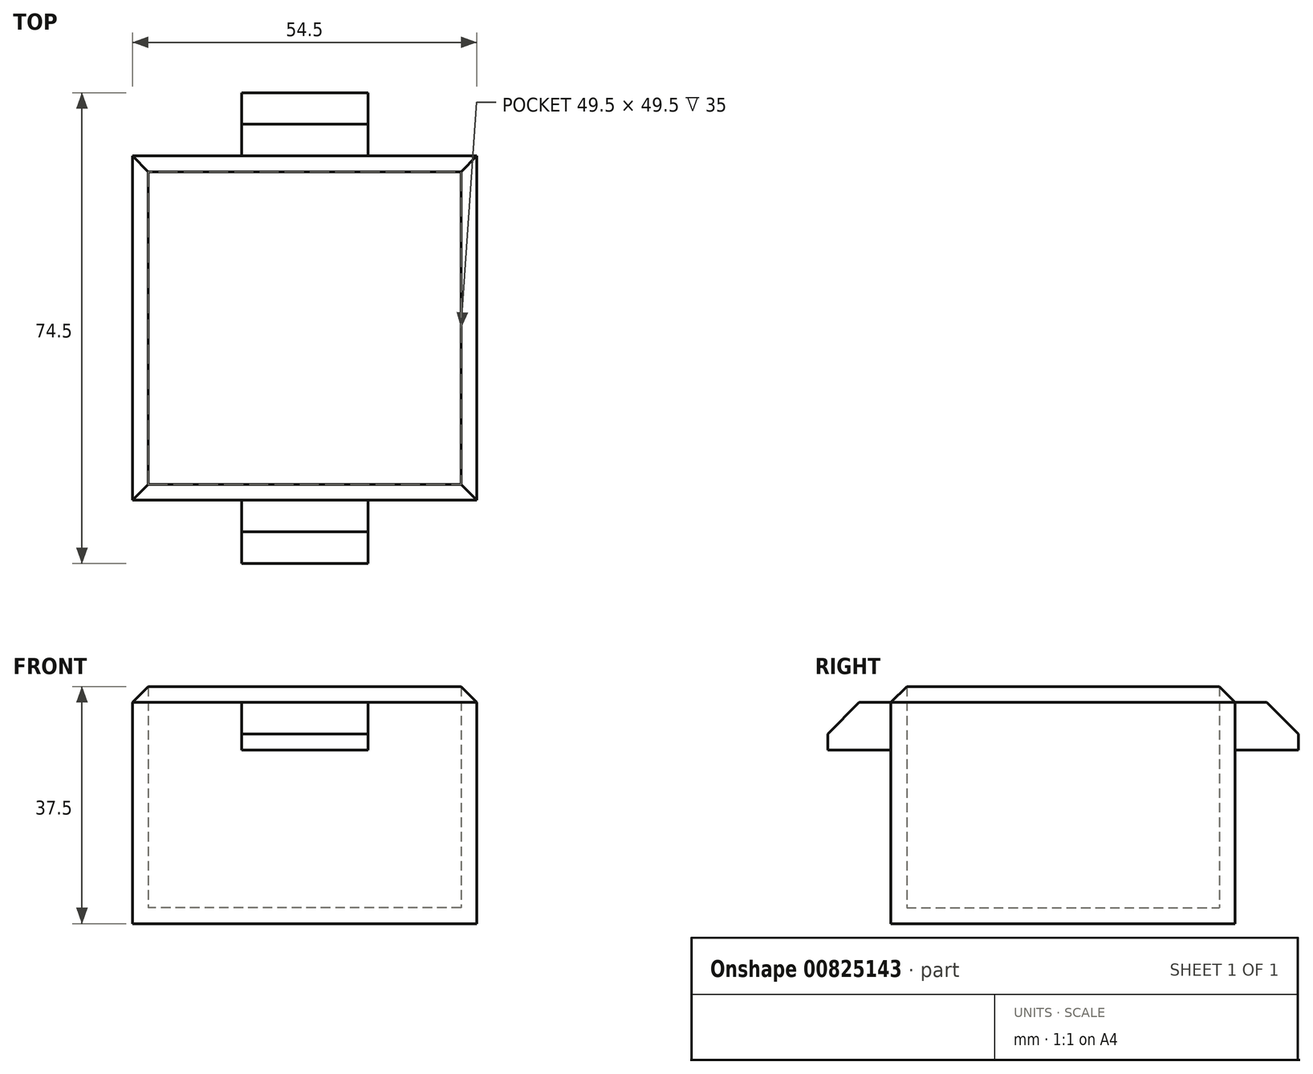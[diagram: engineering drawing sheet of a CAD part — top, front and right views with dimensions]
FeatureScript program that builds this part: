
annotation { "Feature Type Name" : "Feature", "Feature Type Description" : "" }
export const myFeature = defineFeature(function(context is Context, id is Id, definition is map)
    precondition{}
    {
        {
            var Q0;
            Q0=qCreatedBy(makeId("Front.planeOp"),FACE);
            var sketch = newSketch(context, id + "F0", { "sketchPlane" : qUnion([Q0])});
            skLineSegment(sketch, "E0.bottom", {"start": v(27.25, 10) * mm, "end": v(-27.25, 10) * mm});
            skLineSegment(sketch, "E0.top", {"start": v(27.25, -10) * mm, "end": v(-27.25, -10) * mm});
            skLineSegment(sketch, "E0.left", {"start": v(27.25, 10) * mm, "end": v(27.25, -10) * mm});
            skLineSegment(sketch, "E0.right", {"start": v(-27.25, 10) * mm, "end": v(-27.25, -10) * mm});
            skPoint(sketch, "E0.middle", {"position": v(0, 0) * mm});
            skSolve(sketch);
        }
        {
            var Q0;
            Q0=makeQuery(id+"F0.imprint","IMPRINT",FACE,{"disambiguationData":[TD([[makeQuery(id+"F0.imprint","IMPRINT",EDGE,{"derivedFrom":sQuery(id+"F0.wireOp",EDGE,"E0.bottom")}),1.0]])]});
            extrude(context, id + "F1", {"entities" : qUnion([Q0]), "depth" : 54.5 * mm, "offsetDistance" : 25 * mm});
        }
        {
            var Q0;
            Q0=makeQuery(id+"F1.opExtrude","SWEPT_FACE",FACE,{"disambiguationData":[OSD([sQuery(id+"F0.wireOp",EDGE,"E0.bottom")])]});
            extrude(context, id + "F2", {"entities" : qUnion([Q0]), "operationType" : NewBodyOperationType.ADD, "depth" : 20 * mm, "offsetDistance" : 25 * mm});
        }
        {
            var Q0;
            Q0=makeQuery(id+"F2.opExtrude","CAP_FACE",FACE,{"disambiguationData":[OSD([sQuery(id+"F0.wireOp",EDGE,"E0.bottom")])],"isStart":false});
            shell(context, id + "F3", {"entities" : qUnion([Q0]), "thickness" : 2.5 * mm});
        }
        {
            var Q0;
            {var subQ0=sQuery(id+"F0.wireOp",EDGE,"E0.bottom");Q0=makeQuery(id+"F2.boolean.opBoolean","MERGE",FACE,{"derivedFrom":[makeQuery(id+"F1.opExtrude","CAP_FACE",FACE,{"disambiguationData":[OSD([subQ0,sQuery(id+"F0.wireOp",EDGE,"E0.top"),sQuery(id+"F0.wireOp",EDGE,"E0.left"),sQuery(id+"F0.wireOp",EDGE,"E0.right")])],"isStart":false}),makeQuery(id+"F2.opExtrude","SWEPT_FACE",FACE,{"disambiguationData":[OSD([subQ0]),TDD([makeQuery(id+"F1.opExtrude","CAP_EDGE",EDGE,{"disambiguationData":[OSD([subQ0])],"isStart":false})])]})]});}
            var sketch = newSketch(context, id + "F4", { "sketchPlane" : qUnion([Q0])});
            skLineSegment(sketch, "E1", {"start": v(0, 0) * mm, "end": v(0, 30) * mm});
            skLineSegment(sketch, "E2", {"start": v(0, 30) * mm, "end": v(0, 25) * mm});
            skLineSegment(sketch, "E3", {"start": v(0, 25) * mm, "end": v(-10, 25) * mm});
            skLineSegment(sketch, "E4", {"start": v(-10, 25) * mm, "end": v(10, 25) * mm});
            skLineSegment(sketch, "E5", {"start": v(10, 25) * mm, "end": v(10, 17.5) * mm});
            skLineSegment(sketch, "E6", {"start": v(10, 17.5) * mm, "end": v(-10, 17.5) * mm});
            skLineSegment(sketch, "E7", {"start": v(-10, 17.5) * mm, "end": v(-10, 25) * mm});
            skSolve(sketch);
        }
        {
            var Q0;
            {var subQ5=sQuery(id+"F4.wireOp",EDGE,"E7");Q0=makeQuery(id+"F4.imprint","IMPRINT",FACE,{"disambiguationData":[TD([[makeQuery(id+"F4.imprint","IMPRINT",EDGE,{"derivedFrom":subQ5}),-1.0]])]});}
            var Q1;
            {var subQ5=sQuery(id+"F4.wireOp",EDGE,"E5");Q1=makeQuery(id+"F4.imprint","IMPRINT",FACE,{"disambiguationData":[TD([[makeQuery(id+"F4.imprint","IMPRINT",EDGE,{"derivedFrom":subQ5}),-1.0]])]});}
            extrude(context, id + "F5", {"entities" : qUnion([Q0, Q1]), "operationType" : NewBodyOperationType.ADD, "depth" : 10 * mm, "offsetDistance" : 25 * mm});
        }
        {
            var Q0;
            {var subQ0=sQuery(id+"F0.wireOp",EDGE,"E0.bottom");Q0=makeQuery(id+"F2.boolean.opBoolean","MERGE",FACE,{"derivedFrom":[makeQuery(id+"F1.opExtrude","CAP_FACE",FACE,{"disambiguationData":[OSD([subQ0,sQuery(id+"F0.wireOp",EDGE,"E0.top"),sQuery(id+"F0.wireOp",EDGE,"E0.left"),sQuery(id+"F0.wireOp",EDGE,"E0.right")])],"isStart":true}),makeQuery(id+"F2.opExtrude","SWEPT_FACE",FACE,{"disambiguationData":[OSD([subQ0]),TDD([makeQuery(id+"F1.opExtrude","CAP_EDGE",EDGE,{"disambiguationData":[OSD([subQ0])],"isStart":true})])]})]});}
            var sketch = newSketch(context, id + "F6", { "sketchPlane" : qUnion([Q0])});
            skLineSegment(sketch, "E8", {"start": v(0, 0) * mm, "end": v(0, 30) * mm});
            skLineSegment(sketch, "E9", {"start": v(0, 30) * mm, "end": v(0, 25) * mm});
            skLineSegment(sketch, "E10.bottom", {"start": v(0, 25) * mm, "end": v(-10, 25) * mm});
            skLineSegment(sketch, "E10.top", {"start": v(0, 17.5) * mm, "end": v(-10, 17.5) * mm});
            skLineSegment(sketch, "E10.left", {"start": v(0, 25) * mm, "end": v(0, 17.5) * mm});
            skLineSegment(sketch, "E10.right", {"start": v(-10, 25) * mm, "end": v(-10, 17.5) * mm});
            skLineSegment(sketch, "E11.bottom", {"start": v(0, 17.5) * mm, "end": v(10, 17.5) * mm});
            skLineSegment(sketch, "E11.top", {"start": v(0, 25) * mm, "end": v(10, 25) * mm});
            skLineSegment(sketch, "E11.left", {"start": v(0, 17.5) * mm, "end": v(0, 25) * mm});
            skLineSegment(sketch, "E11.right", {"start": v(10, 17.5) * mm, "end": v(10, 25) * mm});
            skSolve(sketch);
        }
        {
            var Q0;
            Q0=makeQuery(id+"F6.imprint","IMPRINT",FACE,{"disambiguationData":[TD([[makeQuery(id+"F6.imprint","IMPRINT",EDGE,{"derivedFrom":sQuery(id+"F6.wireOp",EDGE,"E10.bottom")}),1.0]])]});
            var Q1;
            Q1=makeQuery(id+"F6.imprint","IMPRINT",FACE,{"disambiguationData":[TD([[makeQuery(id+"F6.imprint","IMPRINT",EDGE,{"derivedFrom":sQuery(id+"F6.wireOp",EDGE,"E11.bottom")}),1.0]])]});
            extrude(context, id + "F7", {"entities" : qUnion([Q0, Q1]), "operationType" : NewBodyOperationType.ADD, "depth" : 10 * mm, "offsetDistance" : 25 * mm});
        }
        {
            var Q0;
            Q0=makeQuery(id+"F7.opExtrude","CAP_EDGE",EDGE,{"disambiguationData":[OSD([sQuery(id+"F6.wireOp",EDGE,"E10.bottom"),sQuery(id+"F6.wireOp",EDGE,"E11.top")])],"isStart":false});
            var Q1;
            Q1=makeQuery(id+"F5.opExtrude","CAP_EDGE",EDGE,{"disambiguationData":[OSD([sQuery(id+"F4.wireOp",EDGE,"E4")])],"isStart":false});
            var Q2;
            {var subQ0=sQuery(id+"F0.wireOp",EDGE,"E0.bottom");Q2=makeQuery(id+"F2.opExtrude","CAP_EDGE",EDGE,{"disambiguationData":[OSD([subQ0]),TDD([makeQuery(id+"F1.opExtrude","CAP_EDGE",EDGE,{"disambiguationData":[OSD([subQ0])],"isStart":true})])],"isStart":false});}
            var Q3;
            Q3=makeQuery(id+"F2.opExtrude","CAP_EDGE",EDGE,{"disambiguationData":[OSD([sQuery(id+"F0.wireOp",EDGE,"E0.bottom"),sQuery(id+"F0.wireOp",EDGE,"E0.right")])],"isStart":false});
            var Q4;
            {var subQ0=sQuery(id+"F0.wireOp",EDGE,"E0.bottom");Q4=makeQuery(id+"F2.opExtrude","CAP_EDGE",EDGE,{"disambiguationData":[OSD([subQ0]),TDD([makeQuery(id+"F1.opExtrude","CAP_EDGE",EDGE,{"disambiguationData":[OSD([subQ0])],"isStart":false})])],"isStart":false});}
            var Q5;
            Q5=makeQuery(id+"F2.opExtrude","CAP_EDGE",EDGE,{"disambiguationData":[OSD([sQuery(id+"F0.wireOp",EDGE,"E0.bottom"),sQuery(id+"F0.wireOp",EDGE,"E0.left")])],"isStart":false});
            chamfer(context, id + "F8", {"entities" : qUnion([Q0, Q1, Q2, Q3, Q4, Q5]), "width" : 5 * mm, "tangentPropagation" : true});
        }
    });
